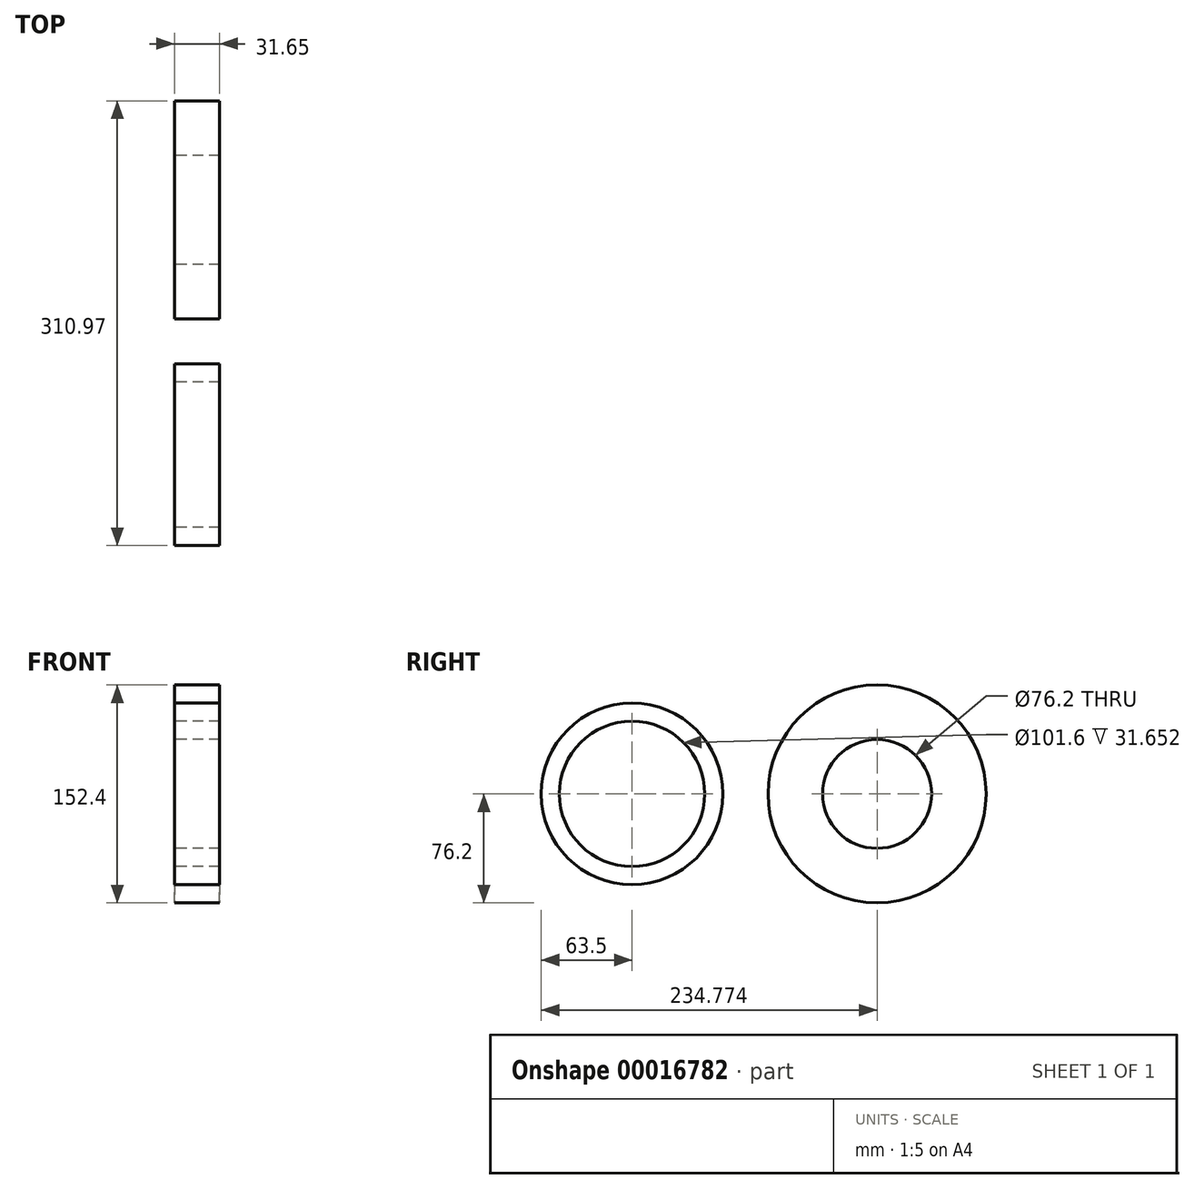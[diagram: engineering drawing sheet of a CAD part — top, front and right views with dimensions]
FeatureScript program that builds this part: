
annotation { "Feature Type Name" : "Feature", "Feature Type Description" : "" }
export const myFeature = defineFeature(function(context is Context, id is Id, definition is map)
    precondition{}
    {
        {
            var Q0;
            Q0=qCreatedBy(makeId("Right.planeOp"),FACE);
            var sketch = newSketch(context, id + "F0", { "sketchPlane" : qUnion([Q0])});
            skCircle(sketch, "E0", {"center": v(0, 0) * mm, "radius": 63.5 * mm});
            skCircle(sketch, "E1", {"center": v(171.27, 0) * mm, "radius": 76.2 * mm});
            skLineSegment(sketch, "E2", {"start": v(0, 63.5) * mm, "end": v(139.58, 69.3) * mm});
            skLineSegment(sketch, "E3", {"start": v(139.58, -69.3) * mm, "end": v(0, -63.55) * mm});
            skCircle(sketch, "E4", {"center": v(0, 0) * mm, "radius": 50.8 * mm});
            skCircle(sketch, "E5", {"center": v(171.27, 0) * mm, "radius": 38.1 * mm});
            skSolve(sketch);
        }
        {
            var Q0;
            Q0=makeQuery(id+"F0.imprint","IMPRINT",FACE,{"disambiguationData":[TD([[makeQuery(id+"F0.imprint","IMPRINT",EDGE,{"derivedFrom":sQuery(id+"F0.wireOp",EDGE,"E0")}),1.0]])]});
            var Q1;
            Q1=makeQuery(id+"F0.imprint","IMPRINT",FACE,{"disambiguationData":[TD([[makeQuery(id+"F0.imprint","IMPRINT",EDGE,{"derivedFrom":sQuery(id+"F0.wireOp",EDGE,"E5")}),-1.0]])]});
            extrude(context, id + "F1", {"entities" : qUnion([Q0, Q1]), "depth" : 31.65 * mm});
        }
        {
            var Q0;
            Q0=sQuery(id+"F0.wireOp",EDGE,"E2");
            var Q1;
            Q1=sQuery(id+"F0.wireOp",EDGE,"E3");
            extrude(context, id + "F2", {"bodyType" : ToolBodyType.SURFACE, "surfaceEntities" : qUnion([Q0, Q1]), "depth" : 26.68 * mm});
        }
    });
